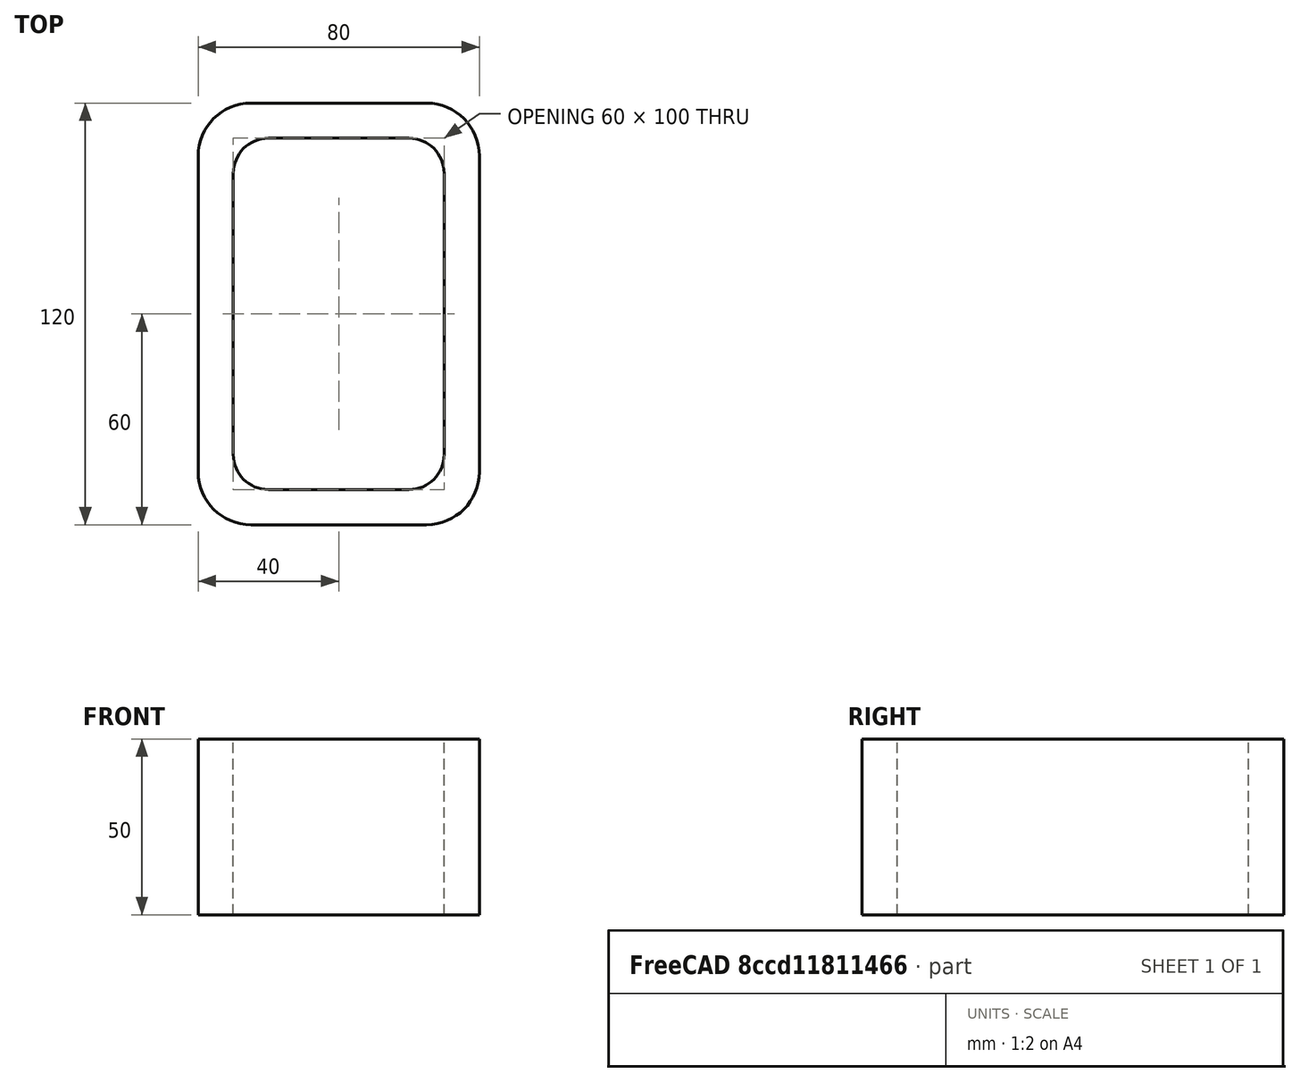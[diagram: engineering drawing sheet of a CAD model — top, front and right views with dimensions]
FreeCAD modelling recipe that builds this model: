
FCSTD DOCUMENT  (FreeCAD 0.15R4671 (Git))
Label: Rectangular hollow section 120x80x10 EN10219 S235JRH
License: All rights reserved
LicenseURL: http://en.wikipedia.org/wiki/All_rights_reserved
objects: Sketcher::SketchObject×1, Part::Extrusion×1
note: 2 computed .brp shape members not serialized (recipe doc carries the construction recipe); baked Part::Feature solids carry a one-line shape summary decoded from their .brp

FEATURE [Sketcher::SketchObject] Sketch
  sketch-geometry (16):
    g0: LineSegment StartX=-20 StartY=50 StartZ=0 EndX=20 EndY=50 EndZ=0
    g1: LineSegment StartX=30 StartY=40 StartZ=0 EndX=30 EndY=-40 EndZ=0
    g2: LineSegment StartX=20 StartY=-50 StartZ=0 EndX=-20 EndY=-50 EndZ=0
    g3: LineSegment StartX=-30 StartY=-40 StartZ=0 EndX=-30 EndY=40 EndZ=0
    g4: LineSegment StartX=-25 StartY=60 StartZ=0 EndX=25 EndY=60 EndZ=0
    g5: LineSegment StartX=40 StartY=45 StartZ=0 EndX=40 EndY=-45 EndZ=0
    g6: LineSegment StartX=25 StartY=-60 StartZ=0 EndX=-25 EndY=-60 EndZ=0
    g7: LineSegment StartX=-40 StartY=-45 StartZ=0 EndX=-40 EndY=45 EndZ=0
    g8: ArcOfCircle CenterX=-20 CenterY=40 CenterZ=0 NormalX=0 NormalY=0 NormalZ=1 Radius=10 StartAngle=1.5708 EndAngle=3.14159
    g9: ArcOfCircle CenterX=20 CenterY=40 CenterZ=0 NormalX=0 NormalY=0 NormalZ=1 Radius=10 StartAngle=0 EndAngle=1.5708
    g10: ArcOfCircle CenterX=20 CenterY=-40 CenterZ=0 NormalX=0 NormalY=0 NormalZ=1 Radius=10 StartAngle=4.71239 EndAngle=6.28319
    g11: ArcOfCircle CenterX=-20 CenterY=-40 CenterZ=0 NormalX=0 NormalY=0 NormalZ=1 Radius=10 StartAngle=3.14159 EndAngle=4.71239
    g12: ArcOfCircle CenterX=25 CenterY=45 CenterZ=0 NormalX=0 NormalY=0 NormalZ=1 Radius=15 StartAngle=0 EndAngle=1.5708
    g13: ArcOfCircle CenterX=25 CenterY=-45 CenterZ=0 NormalX=0 NormalY=0 NormalZ=1 Radius=15 StartAngle=4.71239 EndAngle=6.28319
    g14: ArcOfCircle CenterX=-25 CenterY=-45 CenterZ=0 NormalX=0 NormalY=0 NormalZ=1 Radius=15 StartAngle=3.14159 EndAngle=4.71239
    g15: ArcOfCircle CenterX=-25 CenterY=45 CenterZ=0 NormalX=0 NormalY=0 NormalZ=1 Radius=15 StartAngle=1.5708 EndAngle=3.14159
  constraints (36):
    c: Horizontal(g2)
    c: Vertical(g3)
    c: Horizontal(g6)
    c: Vertical(g7)
    c: Tangent(g3,g8) = 1.5708
    c: Tangent(g0,g8) = 1.5708
    c: Tangent(g0,g9) = 1.5708
    c: Tangent(g1,g9) = 1.5708
    c: Tangent(g1,g10) = 1.5708
    c: Tangent(g2,g10) = 1.5708
    c: Tangent(g2,g11) = 1.5708
    c: Tangent(g3,g11) = 1.5708
    c: Tangent(g4,g12) = 1.5708
    c: Tangent(g5,g12) = 1.5708
    c: Tangent(g5,g13) = 1.5708
    c: Tangent(g6,g13) = 1.5708
    c: Tangent(g6,g14) = 1.5708
    c: Tangent(g7,g14) = 1.5708
    c: Tangent(g7,g15) = 1.5708
    c: Tangent(g4,g15) = 1.5708
    c: Equal(g9,g8)
    c: Equal(g9,g11)
    c: Equal(g9,g10)
    c: Equal(g12,g15)
    c: Equal(g12,g14)
    c: Equal(g12,g13)
    c: Symmetric(g4,g6,g-1)
    c: Symmetric(g7,g5,g-2)
    c: DistanceY(g4,g6) = -120
    c: DistanceX(g7,g5) = 80
    c: Symmetric(g3,g1,g-2)
    c: Symmetric(g0,g2,g-1)
    c: DistanceY(g0,g4) = 10
    c: DistanceX(g5,g1) = -10
    c: Radius(g9) = 10
    c: Radius(g12) = 15
FEATURE [Part::Extrusion] Extrude  label="Rectangular hollow section 120x80x10 EN10219 S235JRH"
  Base = -> Sketch
  Dir = (0,0,50)
  Solid = true
